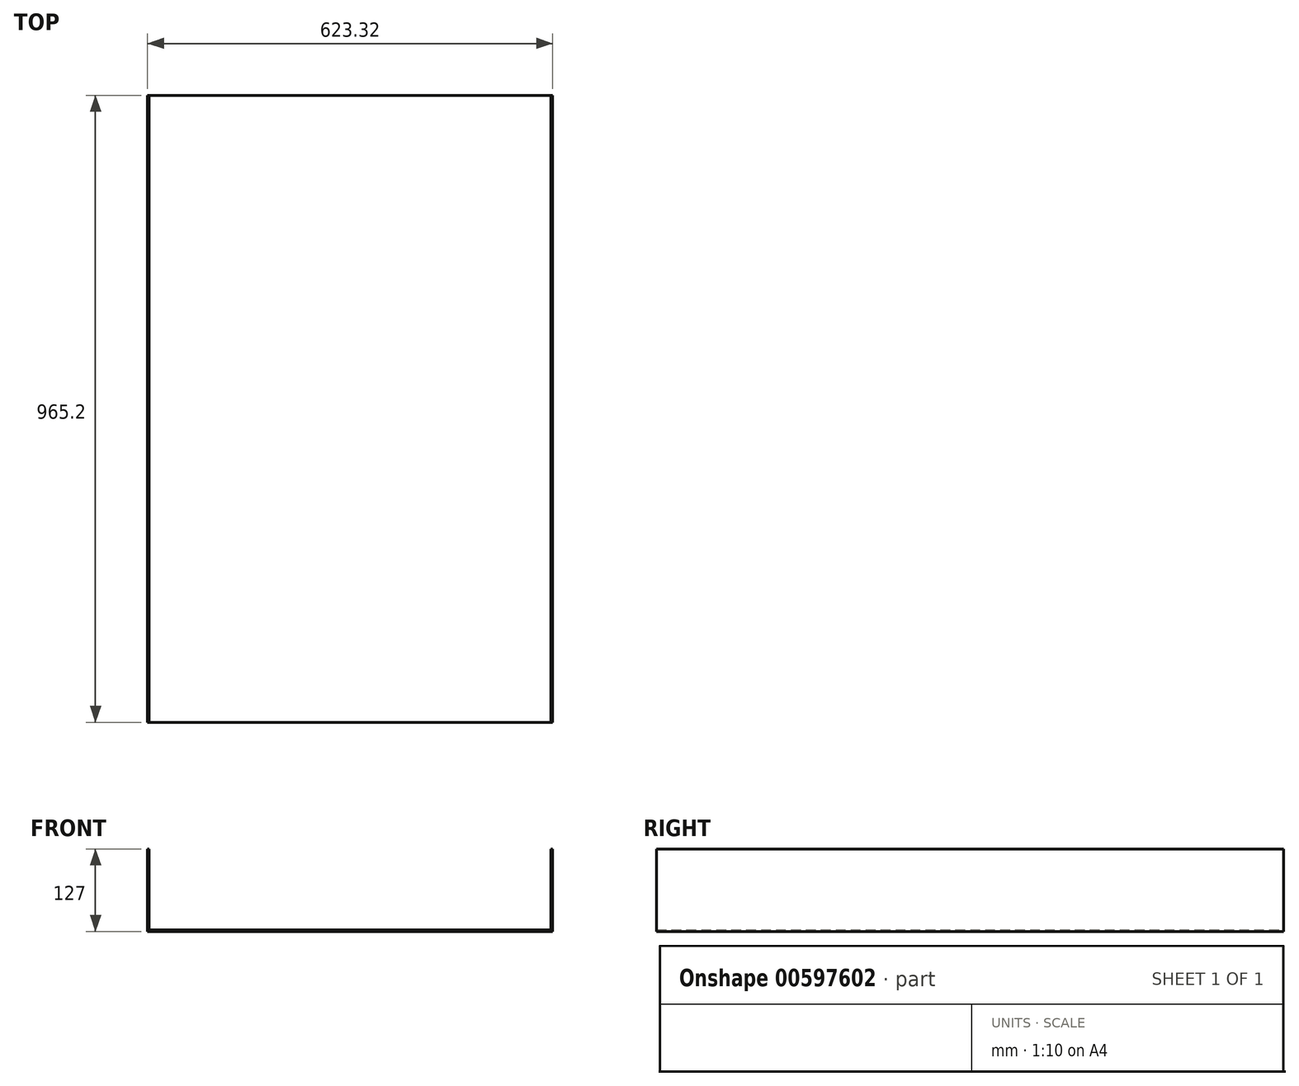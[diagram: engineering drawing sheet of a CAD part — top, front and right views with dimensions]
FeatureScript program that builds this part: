
annotation { "Feature Type Name" : "Feature", "Feature Type Description" : "" }
export const myFeature = defineFeature(function(context is Context, id is Id, definition is map)
    precondition{}
    {
        {
            var Q0;
            Q0=qCreatedBy(makeId("Front.planeOp"),FACE);
            var sketch = newSketch(context, id + "F0", { "sketchPlane" : qUnion([Q0])});
            skLineSegment(sketch, "E0", {"start": v(2.29, 127) * mm, "end": v(2.29, 2.29) * mm});
            skLineSegment(sketch, "E1", {"start": v(2.29, 2.29) * mm, "end": v(621.03, 2.29) * mm});
            skLineSegment(sketch, "E2", {"start": v(621.03, 2.29) * mm, "end": v(621.03, 127) * mm});
            skLineSegment(sketch, "E3.0", {"start": v(623.32, 0) * mm, "end": v(623.32, 127) * mm});
            skLineSegment(sketch, "E3.1", {"start": v(0, 0) * mm, "end": v(623.32, 0) * mm});
            skLineSegment(sketch, "E3.2", {"start": v(0, 127) * mm, "end": v(0, 0) * mm});
            skLineSegment(sketch, "E4", {"start": v(621.03, 127) * mm, "end": v(623.32, 127) * mm});
            skLineSegment(sketch, "E5", {"start": v(2.29, 127) * mm, "end": v(0, 127) * mm});
            skSolve(sketch);
        }
        {
            var Q0;
            Q0=makeQuery(id+"F0.imprint","IMPRINT",FACE,{"disambiguationData":[TD([[makeQuery(id+"F0.imprint","IMPRINT",EDGE,{"derivedFrom":sQuery(id+"F0.wireOp",EDGE,"E0")}),-1.0]])]});
            extrude(context, id + "F1", {"entities" : qUnion([Q0]), "depth" : 965.2 * mm, "offsetDistance" : 25.4 * mm});
        }
    });
